# Revit family: 1401a_omni_bp_dt
name_source: partatom
category: Communication Devices
units: mm (PartAtom-declared; Revit-internal decimal feet)

## family parameters
Cut with Voids When Loaded = No
Host = Face
Maintain Annotation Orientation = No
OmniClass Number = 23.85.80.11.27
OmniClass Title = Lighting Controls
Part Type = Normal
Room Calculation Point = No
Round Connector Dimension = Use Diameter
Shared = Yes

## types (1)
- 1401a_omni_bp_dt
    Assembly Code = D5090
    Certifications = UL and cUL listed
    Coverage = 500 - 2000 sq ft, based on model
    Default Elevation = 48 "
    Description = The OMNIDTBP1277 line voltage ceiling sensor combines ultrasonic (US)
and passive infrared (PIR) technologies to turn lighting on and off based on
occupancy. This dual technology provides accurate turn-ons while virtually
eliminating false-offs.
    Features = IntelliDAPT self-adaptive technology - no manual adjustment required 
All-digital dual technology (ultrasonic [US] and passive infrared [PIR]) sensor 
Non-volatile memory for sensor settings
500–2,000 square-foot coverage area (depending on model)
Self-contained power supply 
Universal voltage (100-277VAC; 50/60 Hz) 
UL and cUL listed 
California Title 24 compliant 
Five-year warranty 
120-277 Vac
    Housing Material = Paint -Matte White
    Manufacturer = NX Lighting Controls
    Model = NX Ceiling Mount Occupancy Sensors employ Passive Infrared
and Ultrasonic sensing technologies to turn lighting on and off based
on occupancy
    Power Requirements = 100-277VAC; 50/60Hz
    Sensing Element = Glass -  White
    Type Comments = OMNI®-BP Line Voltage Dual Technology
    URL = https://www.currentlighting.com
    Warranty = 5-Years Warranty
    Width = 4.5 "

## geometry (parser evidence)
native form markers: Sweep x2
no freeform markers — native parametric forms only
